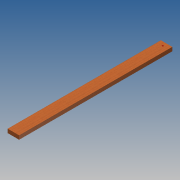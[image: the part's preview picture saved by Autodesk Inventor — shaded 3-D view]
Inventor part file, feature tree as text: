
AUTODESK INVENTOR PART (.ipt)
format: ipt  version: 2014 SP1 (Build 180222100, 222)  size: 87,040 bytes
history: native  units: in
note: dims shown in document units (in); Inventor stores cm internally (conversion verified against a paired STEP export)
features: extrude x2, sketch x2
ambient origin geometry x8: Origin, YZ Plane, XZ Plane, XY Plane, X Axis, Y Axis, Z Axis, Center Point
bodies: Solid1 (feature_tree)
feature tree (4):
  extrude  "Extrusion1"  Depth=1.4961in
  extrude  "Extrusion2"  Depth=0.0394in TaperAngle=0.0deg
  sketch  "Sketch1"  dims[d0=4.4882in d1=1.4961in]
  sketch  "Sketch3"  dims[d2=60.0in d3=0.0in d21=0.0394in d22=0.0in d23=1.4961in d24=0.5906in]
